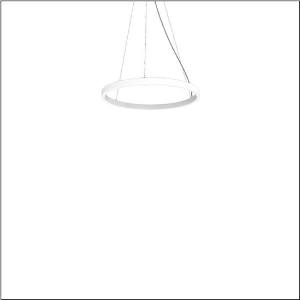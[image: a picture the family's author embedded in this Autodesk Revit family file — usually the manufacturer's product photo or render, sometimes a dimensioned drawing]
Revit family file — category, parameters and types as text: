
# Revit family: silica_r__21_ring-o_5pjbo1d1004a_fa3a
name_source: partatom
category: Lighting Fixtures
units: mm (PartAtom-declared; Revit-internal decimal feet)

## family parameters
Cut with Voids When Loaded = No
Host = Face
Light Source = No
Part Type = Normal
Room Calculation Point = No
Round Connector Dimension = Use Diameter
Shared = No

## types (1)
- Silica® 21 Ring-O (1 x LED, 3740 lm, 60 W, 3000K)
    Apparent Load = 60 VA
    CIE Flux Codes = 2 16 49 50 100
    Color Rendering = 80
    Color Temperature = 3000K
    Default Elevation = 1800 mm
    Description = Silica® 21 Ring-O, suspended luminaire, of PMMA, frosted, light emission: outer ring side luminous distribution, primary light characteristic: symmetric, installation type: suspended mounting, LED, rated luminous flux: 3.744lm, luminous efficacy: 62lm/W, light colour: 830, colour temperature: 3000K, with terminal, 5-pole, mains connection: 230V, AC/DC, 0/50..60Hz, rated input power: 60W, housing, of extruded aluminium section, traffic white (RAL 9016), diameter: 610mm, ceiling canopy, traffic white (RAL 9016), protection rating (lamp compartment): IP40, insulation class (complete): insulation class I (protective earthing), certification: CE, impact resistance: IK02, permissible operating ambient temperature: 0..+35°C, packaging unit: 1 piece
    Height = 48 mm  [stored 0.15748 ft]
    Lamp = 1 x LED
    Lamp Light Flux = 3740 lm
    Lamp Power = 60 W
    Lamp count = 1
    Length = 610 mm
    Luminous efficacy = 62 lm/W
    Manufacturer = Siteco
    ModVariant = No
    Model = 5PJBO1D1004A
    Mounting Place = Ceiling
    Mounting Type = Pendant
    Number of Poles = 1
    OnlyDefault = Yes
    Power Factor = 1
    Product Name = Silica® 21 Ring-O
    Product group = suspended luminaire
    ProductGroupID = 904
    Protection Class = Protection class I
    Protection Degree = IP 40
    RLX_Detail_Level = 1
    RLX_Emergency_Light_Flux = 0 lm
    RLX_Emergency_Type = 0
    RLX_Emergency_Type_DB = No
    RlxData = <blob elided: 10581 chars, md5=5a5ee8b7>
    Socket = socket
    Standby Power = 0 W
    System Light Flux = 3740 lm
    System Power = 60 W
    Type Comments = Product without accessories
    Type Image = l_1258379.jpg
    URL = http://relux.com
    VarID = ---
    Voltage = 0 V
    Weight = 0.00 kg
    Width = 0 mm  [stored 0 ft]

note: [stored X ft] marks values corroborated as IEEE doubles in the binary element streams (Revit-internal decimal feet)

## geometry (parser evidence)
native form markers: Sweep x15
no freeform markers — native parametric forms only
